# Revit family: ROTADO_РотационноДинамическийДефлектор_RDD
name_source: partatom
category: Воздухораспределители
units: mm (PartAtom-declared; Revit-internal decimal feet)

## family parameters
Всегда вертикально = Да
На основе рабочей плоскости = Нет
Общий = Нет
При загрузке вырезать с полостями = Нет
Размер круглого соединителя = Использовать диаметр
Тип детали = Нормальный
Точка расчета площади = Нет

## types (9) — shared parameters
ADSK_URL документации изделия = https://rotado.ru
ADSK_URL страницы изделия = https://rotado.ru
ADSK_Версия Revit = 2019
ADSK_Единица измерения = шт.
ADSK_Завод-изготовитель = ROTADO
ADSK_Классификация нагрузок = Прочее
ADSK_Количество = 1
ADSK_Количество фаз = 1
ADSK_Коэффициент мощности = 0.95
ADSK_Материал = ROTADO_Сталь_Нержавеющая_Оцинкованная
ADSK_Наименование = Ротационно-динамический дефлектор
ADSK_Напряжение = 220 В
H_2 = 190 мм
URL = https://rotado.ru
Изготовитель = ROTADO
Описание = Ротационно-динамический дефлектор — устройство, которое имеет небольшой двигатель и работает как от силы ветра, так и по механическому побуждению.
Производитель_Контакты_Телефон = 88007002460

## per-type parameters (varying)
| type | ADSK_Масса | ADSK_Масса_Текст | ADSK_Номинальная мощность | ADSK_Полная мощность | ADSK_Размер_Высота | ADSK_Размер_Диаметр | ADSK_Размер_Длина | ADSK_Размер_Ширина | D_1 | D_2 | H_1 | Высота_ламель |
| RDD-300 | 6 | 6 | 18 Вт | 19 В·А | 452 мм | 300 мм | 430 мм | 430 мм | 302 мм | 430 мм | 452 мм | 220 мм |
| RDD-315 | 6 | 6 | 18 Вт | 19 В·А | 445 мм | 315 мм | 430 мм | 430 мм | 317 мм | 430 мм | 445 мм | 213 мм |
| RDD-355 | 6 | 6 | 18 Вт | 19 В·А | 445 мм | 355 мм | 456 мм | 456 мм | 357 мм | 456 мм | 445 мм | 213 мм |
| RDD-400 | 8 | 8 | 25 Вт | 26 В·А | 510 мм | 400 мм | 611 мм | 611 мм | 402 мм | 611 мм | 510 мм | 278 мм |
| RDD-450 | 8 | 8 | 25 Вт | 26 В·А | 510 мм | 450 мм | 620 мм | 620 мм | 452 мм | 620 мм | 510 мм | 278 мм |
| RDD-500 | 8 | 8 | 25 Вт | 26 В·А | 490 мм | 500 мм | 630 мм | 630 мм | 502 мм | 630 мм | 490 мм | 258 мм |
| RDD-600 | 12 | 12 | 34 Вт | 36 В·А | 590 мм | 600 мм | 850 мм | 850 мм | 602 мм | 850 мм | 590 мм | 358 мм |
| RDD-680 | 12 | 12 | 34 Вт | 36 В·А | 590 мм | 680 мм | 860 мм | 860 мм | 682 мм | 860 мм | 590 мм | 358 мм |
| RDD-800 | 14 | 14 | 34 Вт | 36 В·А | 590 мм | 800 мм | 965 мм | 965 мм | 802 мм | 965 мм | 590 мм | 358 мм |

note: column(s) folded — value = type name in every type: ADSK_Марка, ADSK_Обозначение
